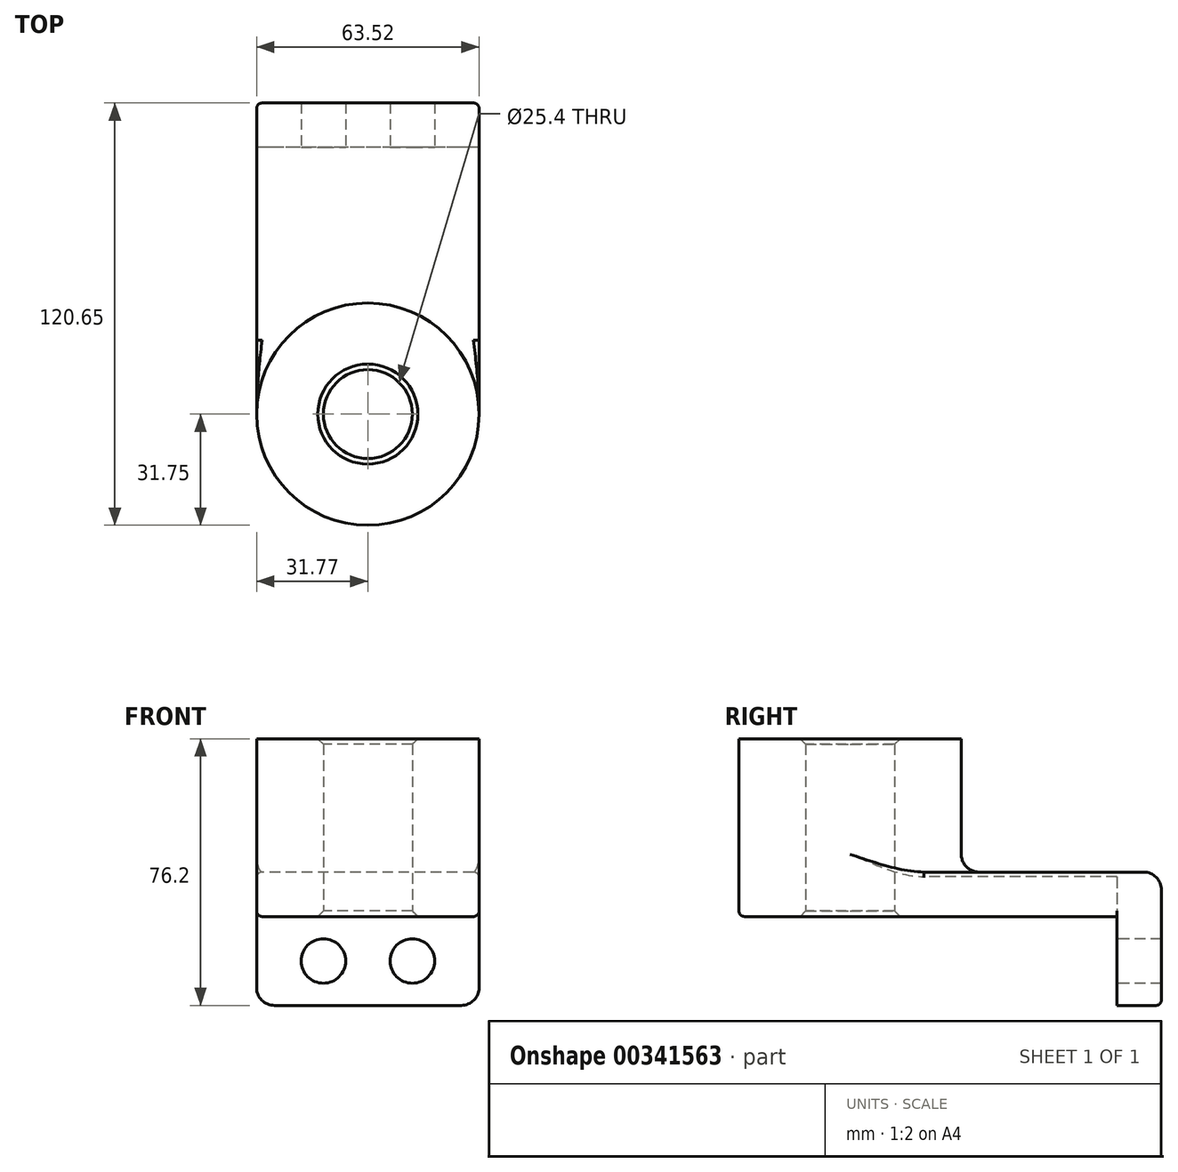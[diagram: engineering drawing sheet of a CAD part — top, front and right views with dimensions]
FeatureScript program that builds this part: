
annotation { "Feature Type Name" : "Feature", "Feature Type Description" : "" }
export const myFeature = defineFeature(function(context is Context, id is Id, definition is map)
    precondition{}
    {
        {
            var Q0;
            Q0=qCreatedBy(makeId("Top.planeOp"),FACE);
            var sketch = newSketch(context, id + "F0", { "sketchPlane" : qUnion([Q0])});
            skLineSegment(sketch, "E0.bottom", {"start": v(31.75, 38.1) * mm, "end": v(-31.75, 38.1) * mm});
            skLineSegment(sketch, "E0.top", {"start": v(31.75, -38.1) * mm, "end": v(-31.75, -38.1) * mm});
            skLineSegment(sketch, "E0.left", {"start": v(31.75, 38.1) * mm, "end": v(31.75, -38.1) * mm});
            skLineSegment(sketch, "E0.right", {"start": v(-31.75, 38.1) * mm, "end": v(-31.75, -38.1) * mm});
            skPoint(sketch, "E0.middle", {"position": v(0, 0) * mm});
            skCircle(sketch, "E1", {"center": v(0, -38.1) * mm, "radius": 31.75 * mm});
            skCircle(sketch, "E2", {"center": v(0, -38.1) * mm, "radius": 12.7 * mm});
            skSolve(sketch);
        }
        {
            var Q0;
            Q0 = qSketchRegion(id + "F0", true);
            extrude(context, id + "F1", {"entities" : qUnion([Q0]), "depth" : 12.7 * mm});
        }
        {
            var Q0;
            {var subQ1=sQuery(id+"F0.wireOp",EDGE,"E0.top");var subQ3=sQuery(id+"F0.wireOp",EDGE,"E2");var subQ4=makeQuery(id+"F0.imprint","INTERSECT",VERTEX,{"disambiguationData":[OD(0.0)],"derivedFrom":[subQ1,subQ3]});Q0=makeQuery(id+"F0.imprint","IMPRINT",FACE,{"disambiguationData":[TD([[makeQuery(id+"F0.imprint","IMPRINT",EDGE,{"disambiguationData":[TD([[subQ4,1.0]])],"derivedFrom":subQ3}),-1.0]])]});}
            var Q1;
            {var subQ1=sQuery(id+"F0.wireOp",EDGE,"E0.top");var subQ3=sQuery(id+"F0.wireOp",EDGE,"E2");var subQ4=makeQuery(id+"F0.imprint","INTERSECT",VERTEX,{"disambiguationData":[OD(0.0)],"derivedFrom":[subQ1,subQ3]});Q1=makeQuery(id+"F0.imprint","IMPRINT",FACE,{"disambiguationData":[TD([[makeQuery(id+"F0.imprint","IMPRINT",EDGE,{"disambiguationData":[TD([[subQ4,-1.0]])],"derivedFrom":subQ3}),-1.0]])]});}
            extrude(context, id + "F2", {"entities" : qUnion([Q0, Q1]), "operationType" : NewBodyOperationType.ADD, "depth" : 50.8 * mm});
        }
        {
            var Q0;
            Q0=makeQuery(id+"F1.opExtrude","SWEPT_FACE",FACE,{"disambiguationData":[OSD([sQuery(id+"F0.wireOp",EDGE,"E0.bottom")])]});
            var sketch = newSketch(context, id + "F3", { "sketchPlane" : qUnion([Q0])});
            skLineSegment(sketch, "E3.bottom", {"start": v(-31.75, 12.7) * mm, "end": v(31.77, 12.7) * mm});
            skLineSegment(sketch, "E3.top", {"start": v(-31.75, -25.4) * mm, "end": v(31.77, -25.4) * mm});
            skLineSegment(sketch, "E3.left", {"start": v(-31.75, 12.7) * mm, "end": v(-31.75, -25.4) * mm});
            skLineSegment(sketch, "E3.right", {"start": v(31.77, 12.7) * mm, "end": v(31.77, -25.4) * mm});
            skCircle(sketch, "E4", {"center": v(-12.7, -12.7) * mm, "radius": 6.35 * mm});
            skLineSegment(sketch, "E5", {"start": v(0, 0) * mm, "end": v(0, -25.4) * mm});
            skCircle(sketch, "E6.MirrorC", {"center": v(12.7, -12.7) * mm, "radius": 6.35 * mm});
            skSolve(sketch);
        }
        {
            var Q0;
            Q0 = qSketchRegion(id + "F3", true);
            extrude(context, id + "F4", {"entities" : qUnion([Q0]), "operationType" : NewBodyOperationType.ADD, "depth" : 12.7 * mm});
        }
        {
            var Q0;
            {var subQ0=sQuery(id+"F0.wireOp",EDGE,"E1");Q0=makeQuery(id+"F2.boolean.opBoolean","INTERSECT",EDGE,{"derivedFrom":[makeQuery(id+"F1.opExtrude","CAP_FACE",FACE,{"disambiguationData":[OSD([sQuery(id+"F0.wireOp",EDGE,"E0.bottom"),sQuery(id+"F0.wireOp",EDGE,"E0.left"),sQuery(id+"F0.wireOp",EDGE,"E0.right"),subQ0,sQuery(id+"F0.wireOp",EDGE,"E2")])],"isStart":false}),makeQuery(id+"F2.opExtrude","SWEPT_FACE",FACE,{"disambiguationData":[OSD([subQ0])]})]});}
            var Q1;
            Q1=makeQuery(id+"F4.opExtrude","CAP_EDGE",EDGE,{"disambiguationData":[OSD([sQuery(id+"F3.wireOp",EDGE,"E3.bottom")])],"isStart":false});
            var Q2;
            Q2=makeQuery(id+"F4.opExtrude","SWEPT_EDGE",EDGE,{"disambiguationData":[OSD([sQuery(id+"F3.wireOp",EDGE,"E3.top"),sQuery(id+"F3.wireOp",EDGE,"E3.right")])]});
            var Q3;
            Q3=makeQuery(id+"F4.opExtrude","SWEPT_EDGE",EDGE,{"disambiguationData":[OSD([sQuery(id+"F3.wireOp",EDGE,"E3.top"),sQuery(id+"F3.wireOp",EDGE,"E3.left")])]});
            fillet(context, id + "F5", {"entities" : qUnion([Q0, Q1, Q2, Q3]), "radius" : 5.08 * mm, "tangentPropagation" : true, "allowEdgeOverflow" : false});
        }
        {
            var Q0;
            Q0=makeQuery(id+"F4.boolean.opBoolean","MERGE",EDGE,{"derivedFrom":[makeQuery(id+"F1.opExtrude","CAP_EDGE",EDGE,{"disambiguationData":[OSD([sQuery(id+"F0.wireOp",EDGE,"E0.left")])],"isStart":false}),makeQuery(id+"F4.opExtrude","SWEPT_EDGE",EDGE,{"disambiguationData":[OSD([sQuery(id+"F3.wireOp",EDGE,"E3.bottom"),sQuery(id+"F3.wireOp",EDGE,"E3.left")])]})]});
            var Q1;
            Q1=makeQuery(id+"F1.opExtrude","CAP_EDGE",EDGE,{"disambiguationData":[OSD([sQuery(id+"F0.wireOp",EDGE,"E0.left")])],"isStart":true});
            fillet(context, id + "F6", {"entities" : qUnion([Q0, Q1]), "radius" : 1.59 * mm, "tangentPropagation" : true, "allowEdgeOverflow" : false});
        }
        {
            var Q0;
            {var subQ0=sQuery(id+"F0.wireOp",EDGE,"E2");Q0=makeQuery(id+"F2.boolean.opBoolean","MERGE",FACE,{"derivedFrom":[makeQuery(id+"F1.opExtrude","SWEPT_FACE",FACE,{"disambiguationData":[OSD([subQ0])]}),makeQuery(id+"F2.opExtrude","SWEPT_FACE",FACE,{"disambiguationData":[OSD([subQ0])]})]});}
            chamfer(context, id + "F7", {"entities" : qUnion([Q0]), "width" : 1.59 * mm, "tangentPropagation" : true});
        }
    });
